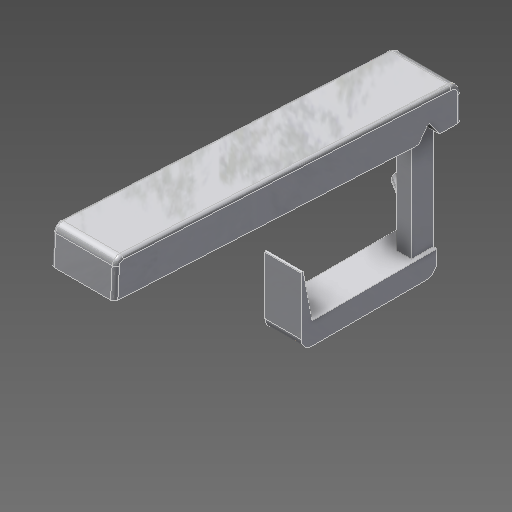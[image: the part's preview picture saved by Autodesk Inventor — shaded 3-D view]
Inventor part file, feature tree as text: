
AUTODESK INVENTOR PART (.ipt)
format: ipt  version: 2020 (Build 240168000, 168)  size: 321,024 bytes
history: native  units: mm
features: extrude x7, fillet x6, other x3, draft x1, chamfer x1
ambient origin geometry x8: Origin, YZ Plane, XZ Plane, XY Plane, X Axis, Y Axis, Z Axis, Center Point
bodies: Solid1 (feature_tree)
feature tree (18):
  other  "Key Sketch"
  extrude  "Upper Key"  Depth=10.0mm
  extrude  "Lower Key"  Depth=1.0mm
  other  "Hinge Cut Sketch"
  extrude  "Hinge Cut"  Depth=10.0mm TaperAngle=0.0deg
  extrude  "Hinge Cut 2"  Depth=3.0mm
  other  "Lever Sketch"
  extrude  "Vertical Lever"  Depth=3.0mm
  extrude  "Horizontal Lever"  Depth=33.6625mm
  extrude  "Spring Hook"  Depth=0.5mm
  draft  "FaceDraft3"
  chamfer  "Chamfer1"  Distance=3.0mm
  fillet  "Fillet9"  Radius=6.0mm
  fillet  "Fillet10"  Radius=4.0mm
  fillet  "Fillet5"  Radius=10.0mm
  fillet  "Fillet4"  [1 undecoded]
  fillet  "Fillet11"  Radius=3.0mm
  fillet  "Fillet14"  Radius=2.3mm
note: 1 required parameter value undecoded (feature->parameter linkage not recoverable at this tier; creation-order binding heuristic only, values carry confidence <= 0.55)
